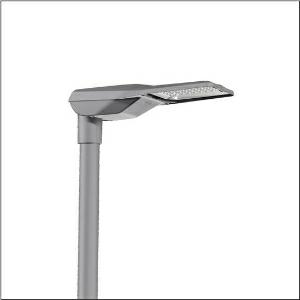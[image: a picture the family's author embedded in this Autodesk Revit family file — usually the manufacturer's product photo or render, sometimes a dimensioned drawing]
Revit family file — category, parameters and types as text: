
# Revit family: streetlight_sl_21_iq_mini___st0_8a_5xe2c41g08hb_fab9
name_source: partatom
category: Lighting Fixtures
units: mm (PartAtom-declared; Revit-internal decimal feet)

## family parameters
Cut with Voids When Loaded = No
Host = Face
Light Source = No
Part Type = Normal
Room Calculation Point = No
Round Connector Dimension = Use Diameter
Shared = No

## types (1)
- --- (1 x LED, 9860 lm, 70.9 W, 4000K)
    Apparent Load = 71 VA
    CIE Flux Codes = 38 75 97 100 100
    Color Rendering = 70
    Color Temperature = 4000K
    Default Elevation = 1800 mm
    Description = Streetlight SL 21 iQ mini, mast luminaire, primary light control with lens, of PMMA, primary optical cover: cover, of toughened safety glass, transparent, light distribution: ST0.8a, light emission: direct distribution, primary light characteristic: asymmetric, installation type: post-top, side-entry, LED, High Power LED, rated luminous flux: 9.860lm, luminous efficacy: 139lm/W, light colour: 740, colour temperature: 4000K, control gear: iQ Street-Remote, control: Street-Remote, Auto-Match, Temp-Guard, Lumen-Switch, Night-Set, Smart-Wire, Light-Fading, Desk-Remote (wireless, voltage-free reading and setting of iQ features in the workshop via application-optimized NFC function/RFID function), optimised constant luminous flux control (CLO 2.0), pre-setting: linear dimming characteristic, mains connection: 220..240V, AC, 50/60Hz, start of lifetime: 71W, end of service life: 75W, reduction: 31W, luminaire housing, of diecast aluminium, powder-coated, SITECO metallic grey (DB 702S), corrosivity category C5 high according to DIN EN ISO 12944, please order mast flange separately, inclination adjustable: 0°, 5°, 10°, 15°, sealing non-destructively replaceable, multi-level sealing system, length: 628mm, width: 235mm, height: 110mm, mast flange for spigot size: 42mm (side-entry): 5XC10008XM4, 60/48mm (side-entry/post-top): 5XC10108XM2, 76/60mm (side-entry/post-top): 5XC10108XM1, mounting height: 4..8m, protection rating (complete): IP66, insulation class (complete): insulation class II (safety insulation), certification: CE, ENEC, ENEC+, VDE, impact resistance: IK10, permissible operating ambient temperature for outdoor applications: -40..+50°C, standard-compliant lighting for roads and squares, packaging unit: 1 piece

Light Distribution: ST0.8a
    Height = 110 mm
    Lamp = 1 x LED
    Lamp Light Flux = 9860 lm
    Lamp Power = 70.9 W
    Lamp count = 1
    Length = 625 mm
    Luminous efficacy = 139 lm/W
    Manufacturer = Siteco
    ModVariant = No
    Model = 5XE2C41G08HB
    Number of Poles = 1
    OnlyDefault = Yes
    Power Factor = 1
    Product Name = Streetlight SL 21 iQ mini | ST0.8a
    Product group = mast luminaire | pylon top
    ProductGroupID = 6100
    Protection Class = Protection class II
    Protection Degree = IP 66
    RLX_Detail_Level = 1
    RLX_Emergency_Light_Flux = 0 lm
    RLX_Emergency_Type = 0
    RLX_Emergency_Type_DB = No
    RlxData = <blob elided: 26325 chars, md5=0070290e>
    Socket = socket
    Standby Power = 0 W
    System Light Flux = 9860 lm
    System Power = 71 W
    Type Comments = factory setting: luminous flux: 100 % | dim-lin: 254 | 711 mA
    Type Image = l_1003519.jpg
    URL = http://relux.com
    VarID = @adj_156805
    Voltage = 0 V
    Weight = 0.00 kg
    Width = 234 mm

## geometry (parser evidence)
native form markers: Blend x4, Sweep x11
no freeform markers — native parametric forms only
